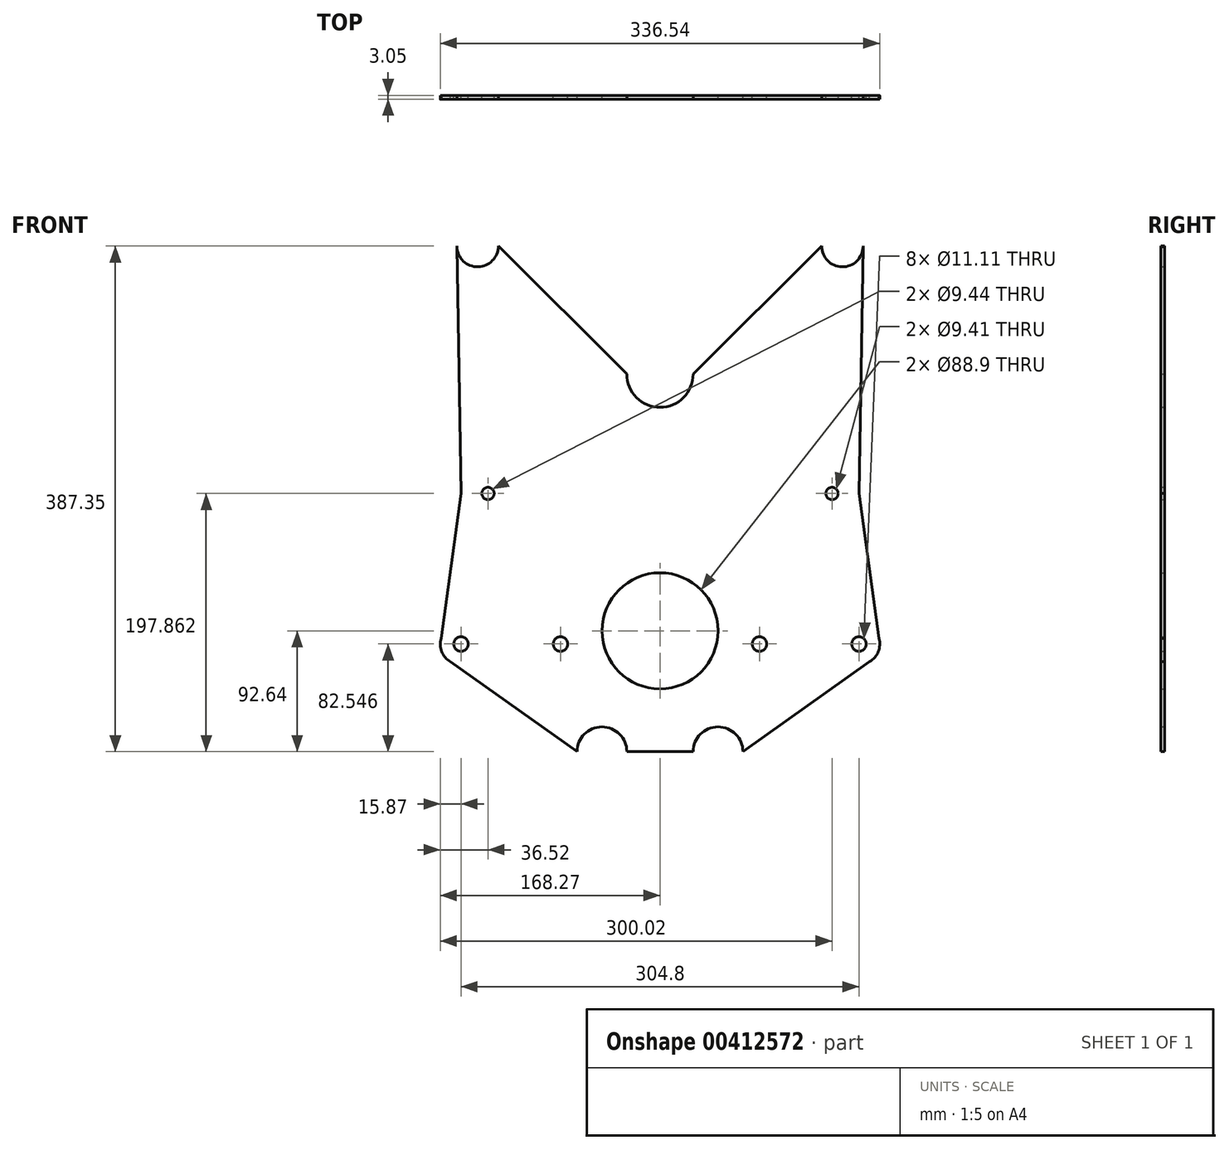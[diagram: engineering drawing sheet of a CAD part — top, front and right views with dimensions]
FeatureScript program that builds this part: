
annotation { "Feature Type Name" : "Feature", "Feature Type Description" : "" }
export const myFeature = defineFeature(function(context is Context, id is Id, definition is map)
    precondition{}
    {
        {
            var Q0;
            Q0=qCreatedBy(makeId("Front.planeOp"),FACE);
            var sketch = newSketch(context, id + "F0", { "sketchPlane" : qUnion([Q0])});
            skPoint(sketch, "E0.middle", {"position": v(0, 0) * mm});
            skPoint(sketch, "E1", {"position": v(20.57, -15.81) * mm});
            skPoint(sketch, "E2", {"position": v(-20.57, -15.81) * mm});
            skLineSegment(sketch, "E3", {"start": v(0, -15.81) * mm, "end": v(152.4, -15.81) * mm, "construction": true});
            skPoint(sketch, "E3.startSnap0", {"position": v(0, -20.57) * mm});
            skLineSegment(sketch, "E4", {"start": v(0, -15.81) * mm, "end": v(-152.4, -15.81) * mm, "construction": true});
            skCircle(sketch, "E5", {"center": v(-152.4, -10.1) * mm, "radius": 5.56 * mm});
            skCircle(sketch, "E6", {"center": v(152.4, -10.1) * mm, "radius": 5.56 * mm});
            skCircle(sketch, "E7", {"center": v(76.2, -10.1) * mm, "radius": 5.56 * mm});
            skCircle(sketch, "E8", {"center": v(-76.2, -10.1) * mm, "radius": 5.56 * mm});
            skPoint(sketch, "E9", {"position": v(-152.4, 105.22) * mm});
            skLineSegment(sketch, "E10", {"start": v(0, 0) * mm, "end": v(0, 140.85) * mm, "construction": true});
            skPoint(sketch, "E10.endSnap0", {"position": v(0, 20.57) * mm});
            skLineSegment(sketch, "E11", {"start": v(-152.4, -10.1) * mm, "end": v(-152.4, -92.64) * mm, "construction": true});
            skLineSegment(sketch, "E12", {"start": v(-152.4, -10.1) * mm, "end": v(-152.4, 294.7) * mm, "construction": true});
            skLineSegment(sketch, "E13", {"start": v(-152.4, 105.22) * mm, "end": v(152.4, 105.22) * mm, "construction": true});
            skCircle(sketch, "E14", {"center": v(-131.75, 105.22) * mm, "radius": 4.72 * mm});
            skCircle(sketch, "E15", {"center": v(131.75, 105.22) * mm, "radius": 4.7 * mm});
            skLineSegment(sketch, "E16", {"start": v(-152.4, -92.64) * mm, "end": v(152.4, -92.64) * mm, "construction": true});
            skPoint(sketch, "E17", {"position": v(-44.45, -92.64) * mm});
            skLineSegment(sketch, "E18", {"start": v(0, -20.57) * mm, "end": v(0, -115.22) * mm, "construction": true});
            skPoint(sketch, "E19", {"position": v(44.45, -92.64) * mm});
            skArc(sketch, "E20", {"start": v(-25.4, -92.64) * mm, "mid": v(-44.45, -73.6) * mm, "end": v(-63.5, -92.64) * mm});
            skArc(sketch, "E21", {"start": v(63.5, -92.64) * mm, "mid": v(44.45, -73.6) * mm, "end": v(25.4, -92.64) * mm});
            skLineSegment(sketch, "E22", {"start": v(-25.4, -92.64) * mm, "end": v(25.4, -92.64) * mm});
            skLineSegment(sketch, "E23", {"start": v(0, 0) * mm, "end": v(0, 293.77) * mm, "construction": true});
            skLineSegment(sketch, "E24", {"start": v(152.4, 294.7) * mm, "end": v(-152.4, 294.7) * mm, "construction": true});
            skPoint(sketch, "E25", {"position": v(-139.7, 294.7) * mm});
            skPoint(sketch, "E26", {"position": v(139.7, 294.7) * mm});
            skArc(sketch, "E27", {"start": v(-155.58, 294.7) * mm, "mid": v(-139.7, 278.83) * mm, "end": v(-123.83, 294.7) * mm});
            skArc(sketch, "E28", {"start": v(123.83, 294.7) * mm, "mid": v(139.7, 278.83) * mm, "end": v(155.58, 294.7) * mm});
            skArc(sketch, "E29", {"start": v(-25.4, 196.65) * mm, "mid": v(0, 171.26) * mm, "end": v(25.4, 196.65) * mm});
            skLineSegment(sketch, "E30", {"start": v(-123.83, 294.7) * mm, "end": v(-25.4, 196.65) * mm});
            skLineSegment(sketch, "E31", {"start": v(123.83, 294.7) * mm, "end": v(25.4, 196.65) * mm});
            skArc(sketch, "E32", {"start": v(160.54, -23.72) * mm, "mid": v(167.15, -15.97) * mm, "end": v(167.68, -5.8) * mm});
            skArc(sketch, "E33", {"start": v(-167.68, -5.8) * mm, "mid": v(-167.15, -15.97) * mm, "end": v(-160.54, -23.72) * mm});
            skLineSegment(sketch, "E34", {"start": v(155.58, 294.7) * mm, "end": v(155.57, 294.17) * mm});
            skLineSegment(sketch, "E35", {"start": v(152.4, 105.22) * mm, "end": v(168.28, -10.1) * mm});
            skLineSegment(sketch, "E36", {"start": v(-155.58, 294.7) * mm, "end": v(-152.4, 105.22) * mm});
            skLineSegment(sketch, "E37", {"start": v(-152.4, 105.22) * mm, "end": v(-168.28, -10.1) * mm});
            skLineSegment(sketch, "E38", {"start": v(155.58, 294.7) * mm, "end": v(152.4, 105.22) * mm});
            skLineSegment(sketch, "E39", {"start": v(162.59, -22.27) * mm, "end": v(63.5, -92.64) * mm});
            skLineSegment(sketch, "E40", {"start": v(-162.59, -22.27) * mm, "end": v(-63.5, -92.64) * mm});
            skCircle(sketch, "E41", {"center": v(0, 0) * mm, "radius": 44.45 * mm});
            skPoint(sketch, "E42.orphan", {"position": v(-20.57, 20.57) * mm});
            skPoint(sketch, "E43.orphan", {"position": v(-20.57, -20.57) * mm});
            skPoint(sketch, "E0.left.start.orphan", {"position": v(20.57, -20.57) * mm});
            skPoint(sketch, "E0.top.start.orphan", {"position": v(20.57, 20.57) * mm});
            skSolve(sketch);
        }
        {
            var Q0;
            Q0=qSketchRegion(id+"F0",true);
            extrude(context, id + "F1", {"entities" : qUnion([Q0]), "depth" : 3.05 * mm});
        }
        {
            var Q0;
            Q0 = qSketchRegion(id + "F0", true);
            extrude(context, id + "F2", {"entities" : qUnion([Q0]), "depth" : 3.05 * mm});
        }
    });
